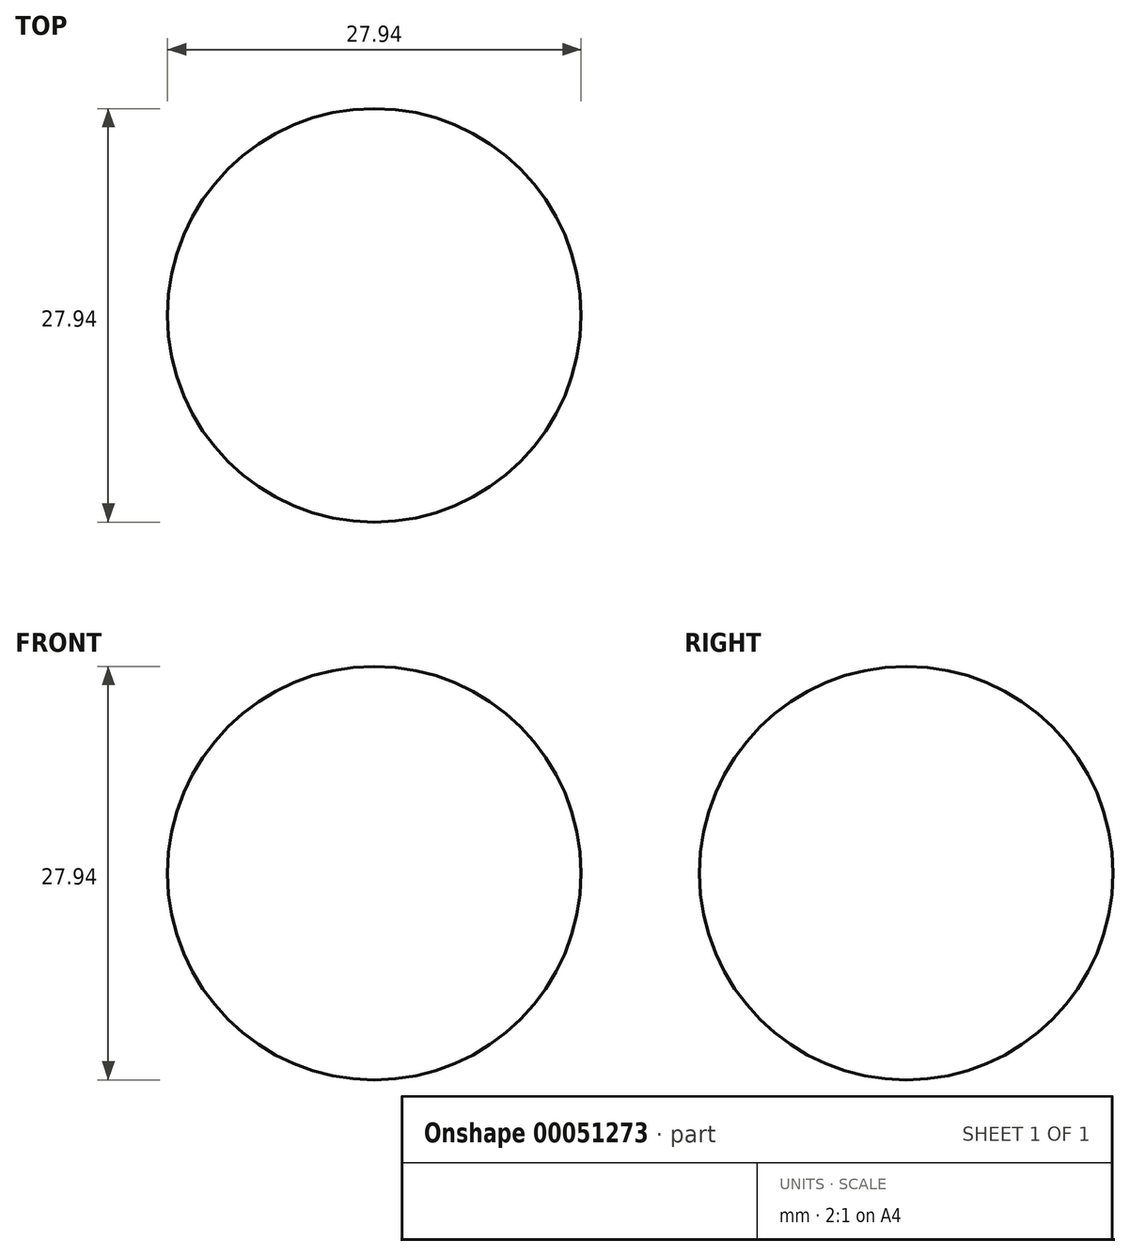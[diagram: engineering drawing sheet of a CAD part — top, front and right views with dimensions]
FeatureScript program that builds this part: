
annotation { "Feature Type Name" : "Feature", "Feature Type Description" : "" }
export const myFeature = defineFeature(function(context is Context, id is Id, definition is map)
    precondition{}
    {
        {
            var Q0;
            Q0=qCreatedBy(makeId("Top.planeOp"),FACE);
            var sketch = newSketch(context, id + "F0", { "sketchPlane" : qUnion([Q0])});
            skArc(sketch, "E0", {"start": v(0, 13.97) * mm, "mid": v(-13.97, 0) * mm, "end": v(0, -13.97) * mm});
            skLineSegment(sketch, "E1", {"start": v(0, -13.97) * mm, "end": v(0, 13.97) * mm});
            skSolve(sketch);
        }
        {
            var Q0;
            Q0=makeQuery(id+"F0.imprint","IMPRINT",FACE,{"disambiguationData":[TD([[makeQuery(id+"F0.imprint","IMPRINT",EDGE,{"derivedFrom":sQuery(id+"F0.wireOp",EDGE,"E0")}),1.0]])]});
            var Q1;
            Q1=sQuery(id+"F0.wireOp",EDGE,"E1");
            revolve(context, id + "F1", {"entities" : qUnion([Q0]), "axis" : qUnion([Q1]), "revolveType" : RevolveType.FULL});
        }
    });
